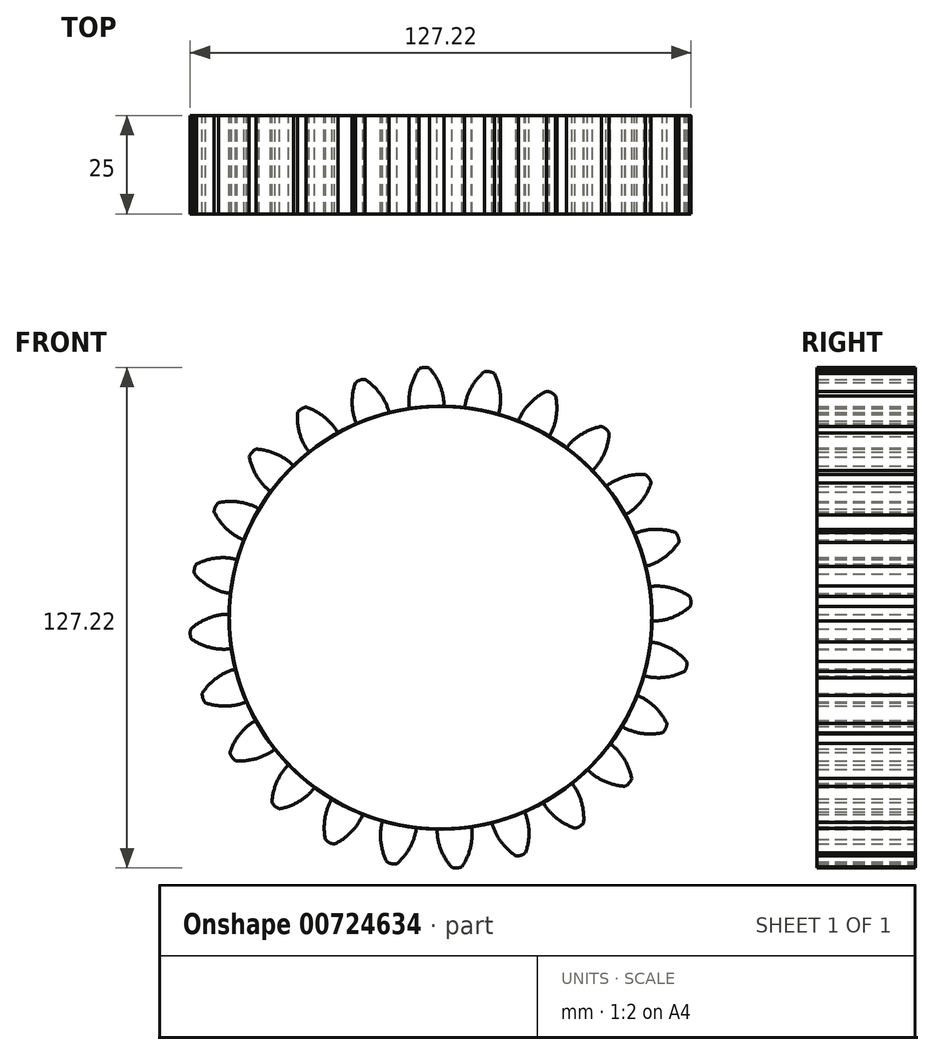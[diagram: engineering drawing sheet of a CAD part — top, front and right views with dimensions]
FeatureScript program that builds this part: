
annotation { "Feature Type Name" : "Feature", "Feature Type Description" : "" }
export const myFeature = defineFeature(function(context is Context, id is Id, definition is map)
    precondition{}
    {
        {
            var Q0;
            Q0=qCreatedBy(makeId("Front.planeOp"),FACE);
            var sketch = newSketch(context, id + "F0", { "sketchPlane" : qUnion([Q0])});
            skCircle(sketch, "E0", {"center": v(0, 0) * mm, "radius": 53.72 * mm});
            skCircle(sketch, "E1", {"center": v(0, 0) * mm, "radius": 58.67 * mm, "construction": true});
            skCircle(sketch, "E2", {"center": v(0, 0) * mm, "radius": 63.5 * mm, "construction": true});
            skLineSegment(sketch, "E3", {"start": v(0, 0) * mm, "end": v(0, 100.95) * mm, "construction": true});
            skLineSegment(sketch, "E4", {"start": v(0, 0) * mm, "end": v(-5.95, 90.82) * mm, "construction": true});
            skLineSegment(sketch, "E5", {"start": v(0, 58.67) * mm, "end": v(-49.43, 58.67) * mm, "construction": true});
            skLineSegment(sketch, "E6", {"start": v(0, 58.67) * mm, "end": v(-58.4, 37.42) * mm, "construction": true});
            skCircle(sketch, "E7", {"center": v(0, 0) * mm, "radius": 55.14 * mm, "construction": true});
            skCircle(sketch, "E8", {"center": v(0, 58.67) * mm, "radius": 14.6 * mm, "construction": true});
            skCircle(sketch, "E9", {"center": v(-13.72, 53.68) * mm, "radius": 14.6 * mm, "construction": true});
            skArc(sketch, "E10", {"start": v(0, 58.67) * mm, "mid": v(-1.2, 61.19) * mm, "end": v(-2.86, 63.44) * mm});
            skArc(sketch, "E11", {"start": v(0.88, 53.71) * mm, "mid": v(0.67, 56.23) * mm, "end": v(0, 58.67) * mm});
            skArc(sketch, "E12.MirrorCS", {"start": v(-7.66, 58.17) * mm, "mid": v(-6.79, 60.82) * mm, "end": v(-5.45, 63.27) * mm});
            skArc(sketch, "E13.MirrorCS", {"start": v(-7.88, 53.14) * mm, "mid": v(-8, 55.67) * mm, "end": v(-7.66, 58.17) * mm});
            skArc(sketch, "E14", {"start": v(-2.86, 63.44) * mm, "mid": v(-4.17, 63.6) * mm, "end": v(-5.45, 63.27) * mm});
            skSolve(sketch);
        }
        {
            var Q0;
            {var subQ0=sQuery(id+"F0.wireOp",EDGE,"E0");var subQ1=makeQuery(id+"F0.imprint","INTERSECT",VERTEX,{"derivedFrom":[subQ0,sQuery(id+"F0.wireOp",EDGE,"E11")]});Q0=makeQuery(id+"F0.imprint","IMPRINT",FACE,{"disambiguationData":[TD([[makeQuery(id+"F0.imprint","IMPRINT",EDGE,{"disambiguationData":[TD([[subQ1,-1.0]])],"derivedFrom":subQ0}),1.0]])]});}
            var Q1;
            Q1=makeQuery(id+"F0.imprint","IMPRINT",FACE,{"disambiguationData":[TD([[makeQuery(id+"F0.imprint","IMPRINT",EDGE,{"derivedFrom":sQuery(id+"F0.wireOp",EDGE,"E10")}),1.0]])]});
            extrude(context, id + "F1", {"entities" : qUnion([Q0, Q1]), "depth" : 25 * mm, "offsetDistance" : 25 * mm});
        }
        {
            var Q0;
            Q0=makeQuery(id+"F1.opExtrude","SWEPT_BODY",BODY,{"disambiguationData":[OSD([sQuery(id+"F0.wireOp",EDGE,"E0"),sQuery(id+"F0.wireOp",EDGE,"E10"),sQuery(id+"F0.wireOp",EDGE,"E11"),sQuery(id+"F0.wireOp",EDGE,"E12.MirrorCS"),sQuery(id+"F0.wireOp",EDGE,"E13.MirrorCS"),sQuery(id+"F0.wireOp",EDGE,"E14")])]});
            var Q1;
            Q1=makeQuery(id+"F1.opExtrude","SWEPT_FACE",FACE,{"disambiguationData":[OSD([sQuery(id+"F0.wireOp",EDGE,"E0")])]});
            circularPattern(context, id + "F2", {"entities" : qUnion([Q0]), "axis" : qUnion([Q1]), "angle" : 360 * degree, "instanceCount" : 24, "equalSpace" : true});
        }
    });
